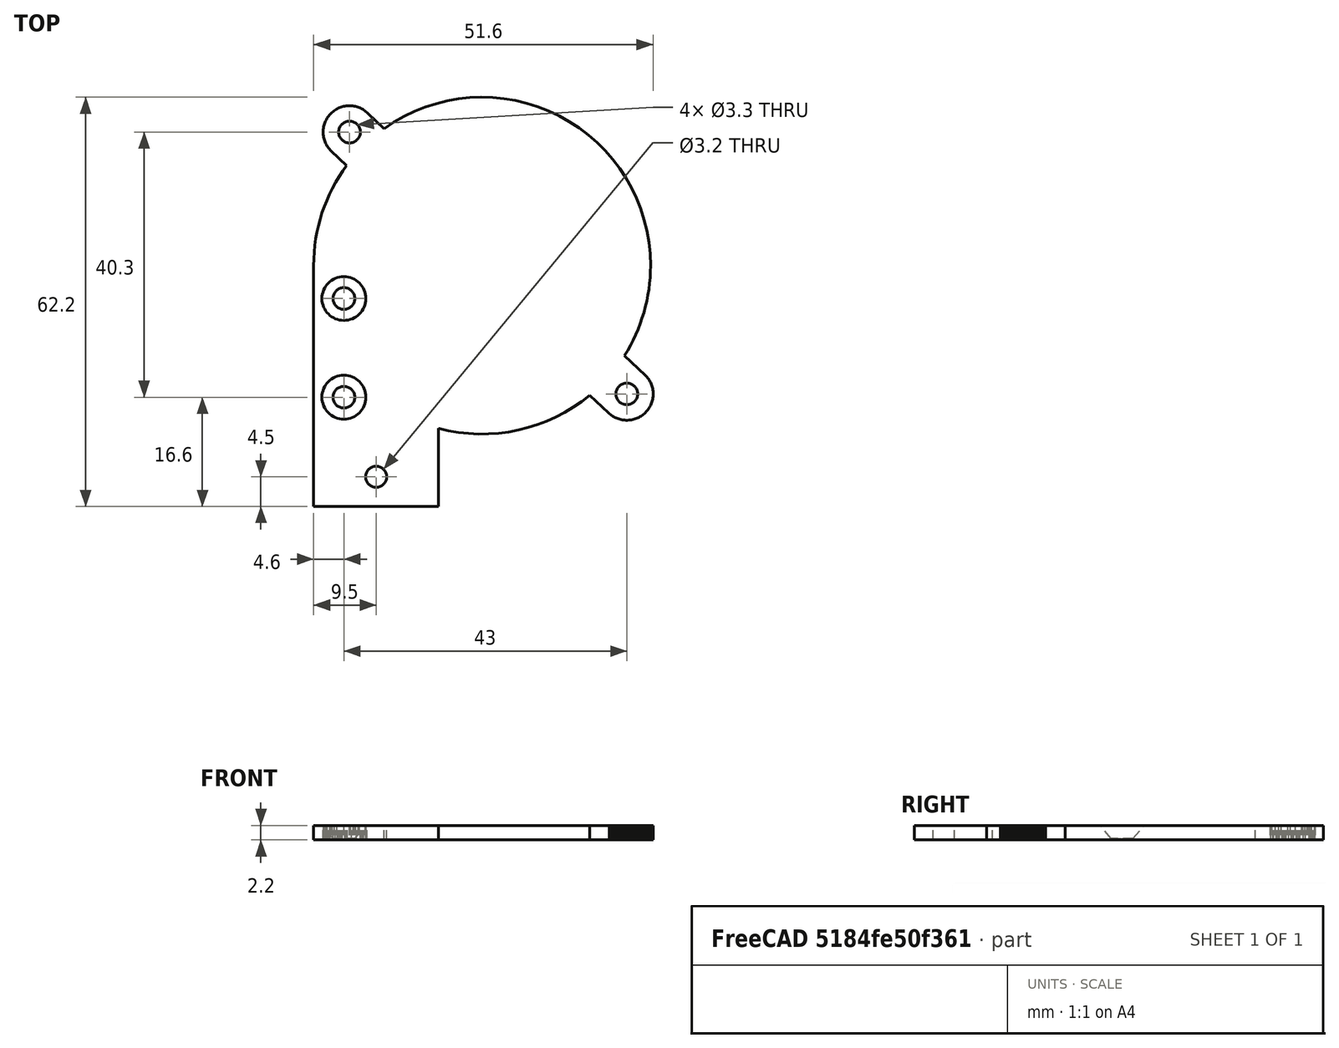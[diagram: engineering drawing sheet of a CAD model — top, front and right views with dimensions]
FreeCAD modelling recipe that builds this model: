
FCSTD DOCUMENT  (FreeCAD 0.19R)
Label: hotend-diamond-fan
License: All rights reserved
LicenseURL: http://en.wikipedia.org/wiki/All_rights_reserved
objects: Part::Cylinder×8, Part::Fuse×6, Part::Box×2, Part::Cone×2, Part::FeaturePython×1, Part::Common×1, Part::MultiFuse×1, Part::Cut×1, PartDesign::FeatureBase×1, PartDesign::Body×1
note: 24 computed .brp shape members not serialized (recipe doc carries the construction recipe); baked Part::Feature solids carry a one-line shape summary decoded from their .brp

FEATURE [Part::Box] cube
  AttacherType = Attacher::AttachEngine3D
  Height = 2.2
  Length = 200
  Placement = pos=(-100,-100,0) rot=(0,0,1;0rad)
  Width = 200
FEATURE [Part::Box] cube001
  AttacherType = Attacher::AttachEngine3D
  Height = 15
  Length = 19
  Placement = pos=(0,-11,0) rot=(0,0,1;0rad)
  Width = 36.6
FEATURE [Part::Cylinder] cylinder
  Angle = 360
  AttacherType = Attacher::AttachEngine3D
  Height = 15
  Radius = 25.6
FEATURE [Part::Cylinder] cylinder001
  Angle = 360
  AttacherType = Attacher::AttachEngine3D
  Height = 15
  Placement = pos=(-20.15,20.3,0) rot=(0,0,1;0rad)
  Radius = 4
FEATURE [Part::Cylinder] cylinder002
  Angle = 360
  AttacherType = Attacher::AttachEngine3D
  Height = 15
  Placement = pos=(22,-19.5,0) rot=(0,0,1;0rad)
  Radius = 4
FEATURE [Part::FeaturePython] hull  # WARN: FeaturePython — macro-defined, semantics opaque (R4)
  Arguments = []
  Children = -> [cylinder001,cylinder002]
  Operation = hull
FEATURE [Part::Fuse] union
  Base = -> cylinder
  Placement = pos=(25.6,25.6,0) rot=(0,0,1;0rad)
  Tool = -> hull
FEATURE [Part::Fuse] union001
  Base = -> cube001
  Tool = -> union
FEATURE [Part::Common] intersection
  Base = -> cube
  Tool = -> union001
FEATURE [Part::Cylinder] cylinder003
  Angle = 360
  AttacherType = Attacher::AttachEngine3D
  Height = 10
  Placement = pos=(-20.15,20.3,-5) rot=(0,0,1;0rad)
  Radius = 1.65
FEATURE [Part::Cylinder] cylinder004
  Angle = 360
  AttacherType = Attacher::AttachEngine3D
  Height = 10
  Placement = pos=(22,-19.5,-5) rot=(0,0,1;0rad)
  Radius = 1.65
FEATURE [Part::Fuse] union002
  Base = -> cylinder003
  Placement = pos=(25.6,25.6,0) rot=(0,0,1;0rad)
  Tool = -> cylinder004
FEATURE [Part::Cylinder] cylinder005
  Angle = 360
  AttacherType = Attacher::AttachEngine3D
  Height = 10
  Placement = pos=(0,0,-5) rot=(0,0,1;0rad)
  Radius = 1.65
FEATURE [Part::Cone] cylinder006
  Angle = 360
  AttacherType = Attacher::AttachEngine3D
  Height = 2.2
  Placement = pos=(0,0,0.2) rot=(0,0,1;0rad)
  Radius1 = 1.65
  Radius2 = 3.5
FEATURE [Part::Fuse] union003
  Base = -> cylinder005
  Placement = pos=(-21,-5,0) rot=(0,0,1;0rad)
  Tool = -> cylinder006
FEATURE [Part::Cylinder] cylinder007
  Angle = 360
  AttacherType = Attacher::AttachEngine3D
  Height = 10
  Placement = pos=(0,0,-5) rot=(0,0,1;0rad)
  Radius = 1.65
FEATURE [Part::Cone] cylinder008
  Angle = 360
  AttacherType = Attacher::AttachEngine3D
  Height = 2.2
  Placement = pos=(0,0,0.2) rot=(0,0,1;0rad)
  Radius1 = 1.65
  Radius2 = 3.5
FEATURE [Part::Fuse] union004
  Base = -> cylinder007
  Placement = pos=(-21,-20,0) rot=(0,0,1;0rad)
  Tool = -> cylinder008
FEATURE [Part::Fuse] Group
  Base = -> union003
  Placement = pos=(25.6,25.6,0) rot=(0,0,1;0rad)
  Tool = -> union004
FEATURE [Part::Cylinder] cylinder009
  Angle = 360
  AttacherType = Attacher::AttachEngine3D
  Height = 10
  Placement = pos=(9.5,-6.5,-5) rot=(0,0,1;0rad)
  Radius = 1.6
FEATURE [Part::MultiFuse] union005
  Shapes = -> [union002,Group,cylinder009]
FEATURE [Part::Cut] difference
  Base = -> intersection
  Refine = true
  Tool = -> union005
FEATURE [PartDesign::FeatureBase] BaseFeature
  BaseFeature = -> difference
FEATURE [PartDesign::Body] Body
  BaseFeature = -> difference
  Group = -> [BaseFeature]
  Origin = -> Origin
  Tip = -> BaseFeature
